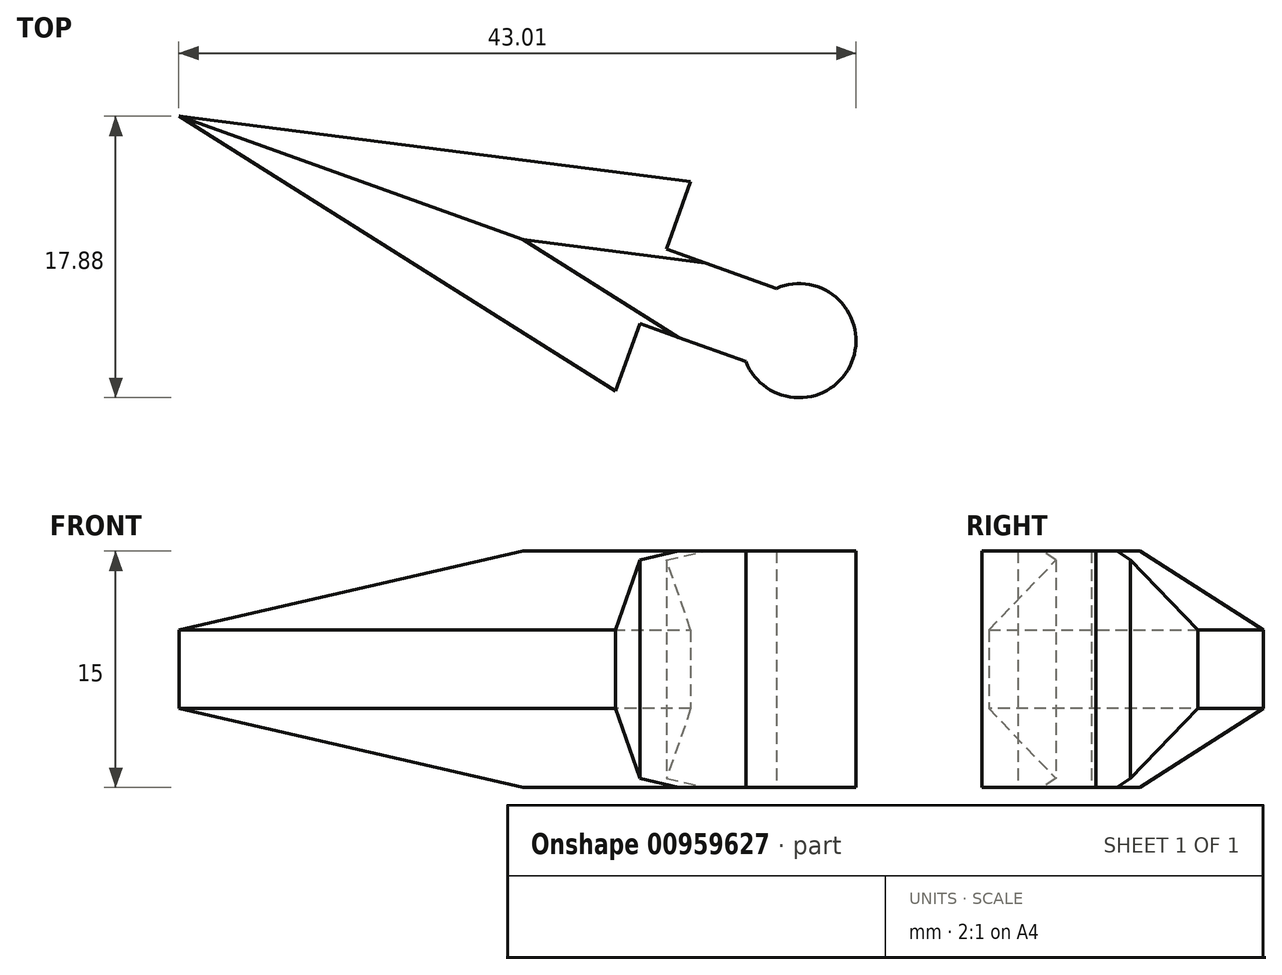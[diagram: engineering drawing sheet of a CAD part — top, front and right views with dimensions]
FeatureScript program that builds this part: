
annotation { "Feature Type Name" : "Feature", "Feature Type Description" : "" }
export const myFeature = defineFeature(function(context is Context, id is Id, definition is map)
    precondition{}
    {
        {
            var Q0;
            Q0=qCreatedBy(makeId("Top.planeOp"),FACE);
            var sketch = newSketch(context, id + "F0", { "sketchPlane" : qUnion([Q0])});
            skCircle(sketch, "E0", {"center": v(-175.92, -10.1) * mm, "radius": 3.62 * mm});
            skLineSegment(sketch, "E1", {"start": v(-179.28, -8.76) * mm, "end": v(-215.3, 4.16) * mm});
            skLineSegment(sketch, "E2", {"start": v(-177.35, -6.78) * mm, "end": v(-184.33, -4.28) * mm});
            skLineSegment(sketch, "E3", {"start": v(-184.33, -4.28) * mm, "end": v(-182.8, 0) * mm});
            skLineSegment(sketch, "E4", {"start": v(-182.8, 0) * mm, "end": v(-215.3, 4.16) * mm});
            skLineSegment(sketch, "E5.MirrorCS", {"start": v(-187.56, -13.29) * mm, "end": v(-215.3, 4.16) * mm});
            skLineSegment(sketch, "E6.MirrorCS", {"start": v(-186.02, -9) * mm, "end": v(-187.56, -13.29) * mm});
            skLineSegment(sketch, "E7.MirrorCS", {"start": v(-179.05, -11.5) * mm, "end": v(-186.02, -9) * mm});
            skSolve(sketch);
        }
        {
            var Q0;
            {var subQ1=sQuery(id+"F0.wireOp",EDGE,"E1");Q0=makeQuery(id+"F0.imprint","IMPRINT",FACE,{"disambiguationData":[TD([[makeQuery(id+"F0.imprint","IMPRINT",EDGE,{"derivedFrom":subQ1}),1.0]])]});}
            var Q1;
            {var subQ1=sQuery(id+"F0.wireOp",EDGE,"E1");Q1=makeQuery(id+"F0.imprint","IMPRINT",FACE,{"disambiguationData":[TD([[makeQuery(id+"F0.imprint","IMPRINT",EDGE,{"derivedFrom":subQ1}),-1.0]])]});}
            var Q2;
            {var subQ0=sQuery(id+"F0.wireOp",EDGE,"E0");var subQ1=makeQuery(id+"F0.imprint","INTERSECT",VERTEX,{"derivedFrom":[subQ0,sQuery(id+"F0.wireOp",EDGE,"E1")]});Q2=makeQuery(id+"F0.imprint","IMPRINT",FACE,{"disambiguationData":[TD([[makeQuery(id+"F0.imprint","IMPRINT",EDGE,{"disambiguationData":[TD([[subQ1,1.0]])],"derivedFrom":subQ0}),1.0]])]});}
            extrude(context, id + "F1", {"entities" : qUnion([Q0, Q1, Q2]), "depth" : 15 * mm, "offsetDistance" : 25 * mm});
        }
        {
            var Q0;
            Q0=makeQuery(id+"F1.opExtrude","CAP_EDGE",EDGE,{"disambiguationData":[OSD([sQuery(id+"F0.wireOp",EDGE,"E5.MirrorCS")])],"isStart":false});
            var Q1;
            Q1=makeQuery(id+"F1.opExtrude","CAP_EDGE",EDGE,{"disambiguationData":[OSD([sQuery(id+"F0.wireOp",EDGE,"E4")])],"isStart":false});
            var Q2;
            Q2=makeQuery(id+"F1.opExtrude","CAP_EDGE",EDGE,{"disambiguationData":[OSD([sQuery(id+"F0.wireOp",EDGE,"E4")])],"isStart":true});
            var Q3;
            Q3=makeQuery(id+"F1.opExtrude","CAP_EDGE",EDGE,{"disambiguationData":[OSD([sQuery(id+"F0.wireOp",EDGE,"E5.MirrorCS")])],"isStart":true});
            chamfer(context, id + "F2", {"entities" : qUnion([Q0, Q1, Q2, Q3]), "width" : 5 * mm, "tangentPropagation" : true});
        }
    });
